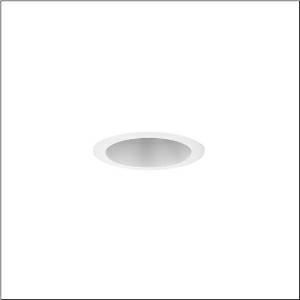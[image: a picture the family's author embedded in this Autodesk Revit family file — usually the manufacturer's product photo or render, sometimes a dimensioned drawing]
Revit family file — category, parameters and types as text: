
# Revit family: lunis_31-l_51dn15ee41b
name_source: partatom
category: Lighting Fixtures
units: mm (PartAtom-declared; Revit-internal decimal feet)

## family parameters
Cut with Voids When Loaded = No
Host = Face
Light Source = No
Part Type = Normal
Room Calculation Point = No
Round Connector Dimension = Use Diameter
Shared = No

## types (1)
- --- (1 x LED, 1750 lm, 12.2 W, 4000K)
    Apparent Load = 12 VA
    CIE Flux Codes = 93 98 100 100 100
    Color Rendering = 80
    Color Temperature = 4000K
    Default Elevation = 1800 mm
    Description = Lunis 31-L, downlight, light control with reflector, light emission: direct distribution, LED rated luminous flux: 1.750lm, light colour: 840, mains connection: 220..240V, AC/DC, 0/50..60Hz, housing, of aluminium, white, protection rating (complete): IP20, protection rating (on room side): IP54, insulation class (complete): insulation class II (safety insulation), certification: CE, ENEC, packaging unit: 1 piece
    Height = 0 mm  [stored 0 ft]
    Lamp = 1 x LED
    Lamp Light Flux = 1750 lm
    Lamp Power = 12.2 W
    Lamp count = 1
    Length = 188 mm  [stored 0.616798 ft]
    Luminous efficacy = 143 lm/W
    Manufacturer = Siteco
    ModVariant = No
    Model = 51DN15EE41B
    Mounting Place = Ceiling
    Mounting Type = Recessed
    Number of Poles = 1
    OnlyDefault = Yes
    Power Factor = 1
    Product Name = Lunis 31-L
    Product group = downlight
    ProductGroupID = 401
    Protection Class = Protection class II
    Protection Degree = IP 20
    RLX_Detail_Level = 1
    RLX_Emergency_Light_Flux = 0 lm
    RLX_Emergency_Type = 0
    RLX_Emergency_Type_DB = No
    RlxData = <blob elided: 22261 chars, md5=f32efbfd>
    Socket = socket
    Standby Power = 0 W
    System Light Flux = 1750 lm
    System Power = 12 W
    Type Comments = individual setting: luminous flux: 100 % | (OFF | ON) | 300 mA
    Type Image = l_1345911.jpg
    URL = http://relux.com
    VarID = @adj_029663
    Voltage = 0 V
    Weight = 0.00 kg
    Width = 0 mm  [stored 0 ft]

note: [stored X ft] marks values corroborated as IEEE doubles in the binary element streams (Revit-internal decimal feet)

## geometry (parser evidence)
native form markers: Blend x4, Sweep x11
no freeform markers — native parametric forms only
